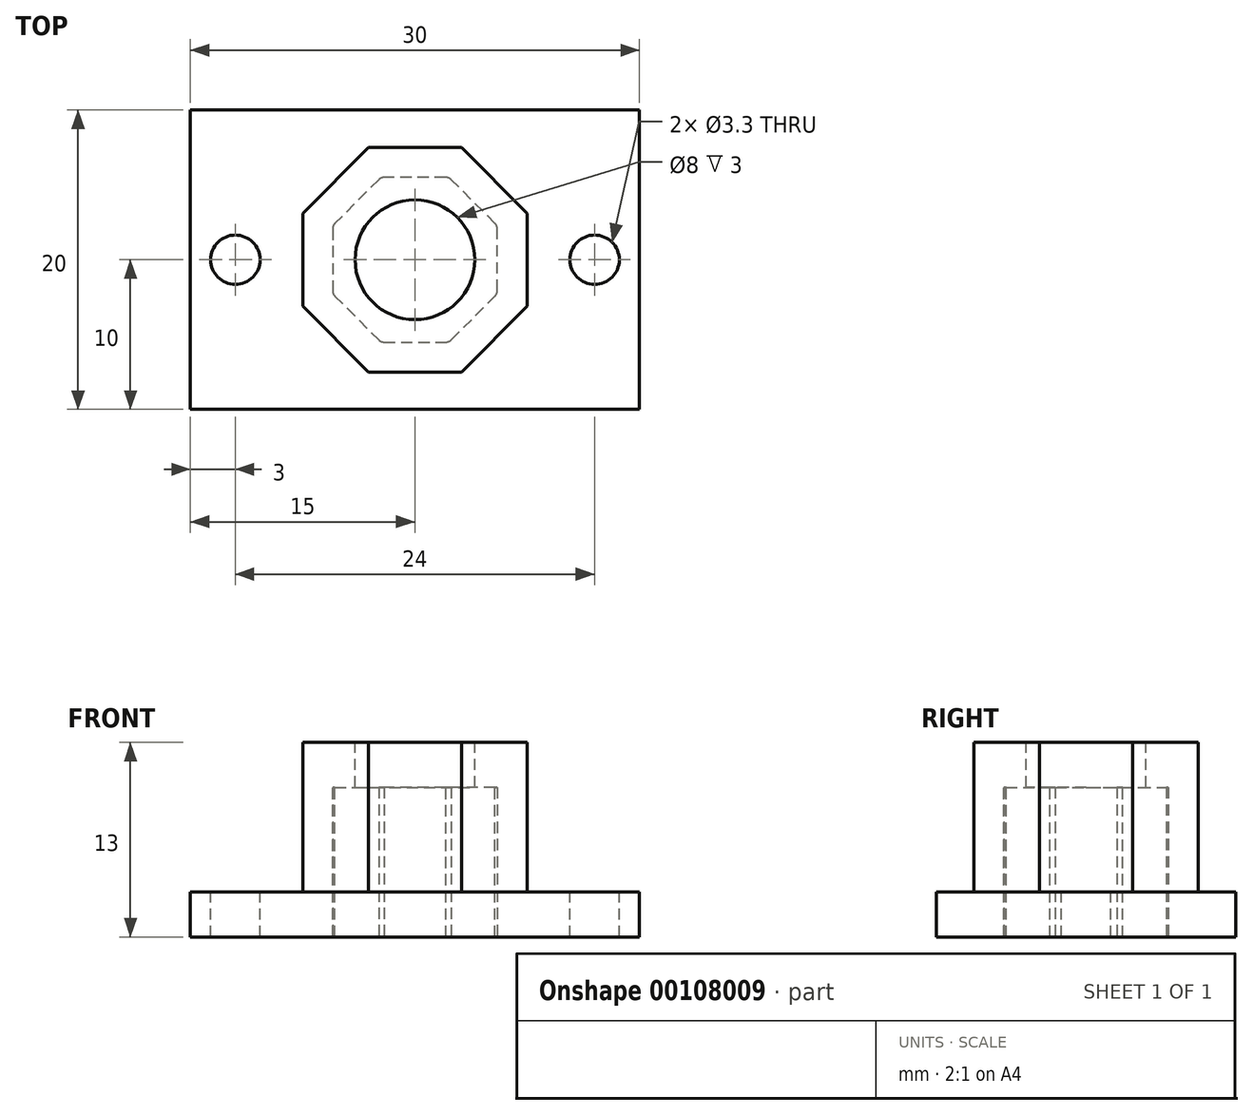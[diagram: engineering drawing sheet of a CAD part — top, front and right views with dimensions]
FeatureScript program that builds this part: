
annotation { "Feature Type Name" : "Feature", "Feature Type Description" : "" }
export const myFeature = defineFeature(function(context is Context, id is Id, definition is map)
    precondition{}
    {
        {
            var Q0;
            Q0=qCreatedBy(makeId("Front.planeOp"),FACE);
            var sketch = newSketch(context, id + "F0", { "sketchPlane" : qUnion([Q0])});
            skLineSegment(sketch, "E0.bottom", {"start": v(15, -1.5) * mm, "end": v(-15, -1.5) * mm});
            skLineSegment(sketch, "E0.top", {"start": v(15, 1.5) * mm, "end": v(-15, 1.5) * mm});
            skLineSegment(sketch, "E0.left", {"start": v(15, -1.5) * mm, "end": v(15, 1.5) * mm});
            skLineSegment(sketch, "E0.right", {"start": v(-15, -1.5) * mm, "end": v(-15, 1.5) * mm});
            skPoint(sketch, "E0.middle", {"position": v(0, 0) * mm});
            skSolve(sketch);
        }
        {
            var Q0;
            Q0 = qSketchRegion(id + "F0", true);
            var Q1;
            Q1 = qSketchRegion(id + "F6", true);
            extrude(context, id + "F1", {"entities" : qUnion([Q0, Q1]), "endBound" : BoundingType.SYMMETRIC, "depth" : 20 * mm});
        }
        {
            var Q0;
            Q0=makeQuery(id+"F1.opExtrude","SWEPT_FACE",FACE,{"disambiguationData":[OSD([sQuery(id+"F0.wireOp",EDGE,"E0.top")])]});
            var sketch = newSketch(context, id + "F2", { "sketchPlane" : qUnion([Q0])});
            skPoint(sketch, "E1", {"position": v(0, 0) * mm});
            skCircle(sketch, "E2.cCircle", {"center": v(0, 0) * mm, "radius": 7.5 * mm, "construction": true});
            skLineSegment(sketch, "E2.0", {"start": v(3.1, -7.5) * mm, "end": v(-3.1, -7.5) * mm});
            skLineSegment(sketch, "E2.1", {"start": v(-3.1, -7.5) * mm, "end": v(-7.5, -3.1) * mm});
            skLineSegment(sketch, "E2.2", {"start": v(-7.5, -3.1) * mm, "end": v(-7.5, 3.1) * mm});
            skLineSegment(sketch, "E2.3", {"start": v(-7.5, 3.1) * mm, "end": v(-3.1, 7.5) * mm});
            skLineSegment(sketch, "E2.4", {"start": v(-3.1, 7.5) * mm, "end": v(3.1, 7.5) * mm});
            skLineSegment(sketch, "E2.5", {"start": v(3.1, 7.5) * mm, "end": v(7.5, 3.1) * mm});
            skLineSegment(sketch, "E2.6", {"start": v(7.5, 3.1) * mm, "end": v(7.5, -3.1) * mm});
            skLineSegment(sketch, "E2.7", {"start": v(7.5, -3.1) * mm, "end": v(3.1, -7.5) * mm});
            skPoint(sketch, "E2.0.midPoint", {"position": v(0, -7.5) * mm});
            skSolve(sketch);
        }
        {
            var Q0;
            Q0 = qSketchRegion(id + "F2", true);
            extrude(context, id + "F3", {"entities" : qUnion([Q0]), "operationType" : NewBodyOperationType.ADD, "depth" : 10 * mm});
        }
        {
            var Q0;
            Q0=makeQuery(id+"F1.opExtrude","SWEPT_FACE",FACE,{"disambiguationData":[OSD([sQuery(id+"F0.wireOp",EDGE,"E0.bottom")])]});
            var sketch = newSketch(context, id + "F4", { "sketchPlane" : qUnion([Q0])});
            skCircle(sketch, "E3.cCircle", {"center": v(0, 0) * mm, "radius": 5.5 * mm, "construction": true});
            skLineSegment(sketch, "E3.0", {"start": v(2.28, -5.5) * mm, "end": v(-2.28, -5.5) * mm});
            skLineSegment(sketch, "E3.1", {"start": v(-2.28, -5.5) * mm, "end": v(-5.5, -2.28) * mm});
            skLineSegment(sketch, "E3.2", {"start": v(-5.5, -2.28) * mm, "end": v(-5.5, 2.28) * mm});
            skLineSegment(sketch, "E3.3", {"start": v(-5.5, 2.28) * mm, "end": v(-2.28, 5.5) * mm});
            skLineSegment(sketch, "E3.4", {"start": v(-2.28, 5.5) * mm, "end": v(2.28, 5.5) * mm});
            skLineSegment(sketch, "E3.5", {"start": v(2.28, 5.5) * mm, "end": v(5.5, 2.28) * mm});
            skLineSegment(sketch, "E3.6", {"start": v(5.5, 2.28) * mm, "end": v(5.5, -2.28) * mm});
            skLineSegment(sketch, "E3.7", {"start": v(5.5, -2.28) * mm, "end": v(2.28, -5.5) * mm});
            skPoint(sketch, "E3.0.midPoint", {"position": v(0, -5.5) * mm});
            skSolve(sketch);
        }
        {
            var Q0;
            Q0=makeQuery(id+"F4.imprint","IMPRINT",FACE,{"disambiguationData":[TD([[makeQuery(id+"F4.imprint","IMPRINT",EDGE,{"derivedFrom":sQuery(id+"F4.wireOp",EDGE,"E3.0")}),-1.0]])]});
            extrude(context, id + "F5", {"entities" : qUnion([Q0]), "operationType" : NewBodyOperationType.REMOVE, "oppositeDirection" : true, "depth" : 10 * mm});
        }
        {
            var Q0;
            Q0=makeQuery(id+"F3.opExtrude","CAP_FACE",FACE,{"disambiguationData":[OSD([sQuery(id+"F2.wireOp",EDGE,"E2.0"),sQuery(id+"F2.wireOp",EDGE,"E2.1"),sQuery(id+"F2.wireOp",EDGE,"E2.2"),sQuery(id+"F2.wireOp",EDGE,"E2.3"),sQuery(id+"F2.wireOp",EDGE,"E2.4"),sQuery(id+"F2.wireOp",EDGE,"E2.5"),sQuery(id+"F2.wireOp",EDGE,"E2.6"),sQuery(id+"F2.wireOp",EDGE,"E2.7")])],"isStart":false});
            var sketch = newSketch(context, id + "F6", { "sketchPlane" : qUnion([Q0])});
            skCircle(sketch, "E4", {"center": v(0, 0) * mm, "radius": 4 * mm});
            skSolve(sketch);
        }
        {
            var Q0;
            Q0=sQuery(id+"F6.wireOp",VERTEX,"E4.center");
            var Q1;
            Q1=makeQuery(id+"F1.opExtrude","SWEPT_BODY",BODY,{"disambiguationData":[OSD([sQuery(id+"F0.wireOp",EDGE,"E0.bottom"),sQuery(id+"F0.wireOp",EDGE,"E0.top"),sQuery(id+"F0.wireOp",EDGE,"E0.left"),sQuery(id+"F0.wireOp",EDGE,"E0.right")])]});
            hole(context, id + "F7", {"style" : HoleStyle.SIMPLE, "endStyle" : HoleEndStyle.THROUGH, "holeDiameter" : 8 * mm, "startFromSketch" : true, "locations" : qUnion([Q0]), "scope" : qUnion([Q1]), "isTappedThrough" : true});
        }
        {
            var Q0;
            Q0=makeQuery(id+"F5.boolean.opBoolean","COPY",EDGE,{"derivedFrom":makeQuery(id+"F5.opExtrude","SWEPT_EDGE",EDGE,{"disambiguationData":[OSD([sQuery(id+"F4.wireOp",EDGE,"E3.4"),sQuery(id+"F4.wireOp",EDGE,"E3.5")])]})});
            fillet(context, id + "F8", {"entities" : qUnion([Q0]), "radius" : 0.5 * mm, "rho" : 0.5, "crossSection" : FilletCrossSection.CONIC, "allowEdgeOverflow" : false});
        }
        {
            var Q0;
            Q0=makeQuery(id+"F5.boolean.opBoolean","COPY",EDGE,{"derivedFrom":makeQuery(id+"F5.opExtrude","SWEPT_EDGE",EDGE,{"disambiguationData":[OSD([sQuery(id+"F4.wireOp",EDGE,"E3.5"),sQuery(id+"F4.wireOp",EDGE,"E3.6")])]})});
            fillet(context, id + "F9", {"entities" : qUnion([Q0]), "radius" : 0.5 * mm, "tangentPropagation" : true, "allowEdgeOverflow" : false});
        }
        {
            var Q0;
            Q0=makeQuery(id+"F5.boolean.opBoolean","COPY",EDGE,{"derivedFrom":makeQuery(id+"F5.opExtrude","SWEPT_EDGE",EDGE,{"disambiguationData":[OSD([sQuery(id+"F4.wireOp",EDGE,"E3.3"),sQuery(id+"F4.wireOp",EDGE,"E3.4")])]})});
            fillet(context, id + "F10", {"entities" : qUnion([Q0]), "radius" : 0.5 * mm, "tangentPropagation" : true, "rho" : 0.5, "crossSection" : FilletCrossSection.CONIC, "allowEdgeOverflow" : false});
        }
        {
            var Q0;
            Q0=makeQuery(id+"F5.boolean.opBoolean","COPY",EDGE,{"derivedFrom":makeQuery(id+"F5.opExtrude","SWEPT_EDGE",EDGE,{"disambiguationData":[OSD([sQuery(id+"F4.wireOp",EDGE,"E3.2"),sQuery(id+"F4.wireOp",EDGE,"E3.3")])]})});
            fillet(context, id + "F11", {"entities" : qUnion([Q0]), "radius" : 0.5 * mm, "tangentPropagation" : true, "rho" : 0.5, "crossSection" : FilletCrossSection.CONIC, "allowEdgeOverflow" : false});
        }
        {
            var Q0;
            Q0=makeQuery(id+"F5.boolean.opBoolean","COPY",EDGE,{"derivedFrom":makeQuery(id+"F5.opExtrude","SWEPT_EDGE",EDGE,{"disambiguationData":[OSD([sQuery(id+"F4.wireOp",EDGE,"E3.1"),sQuery(id+"F4.wireOp",EDGE,"E3.2")])]})});
            fillet(context, id + "F12", {"entities" : qUnion([Q0]), "radius" : 0.5 * mm, "tangentPropagation" : true, "rho" : 0.5, "crossSection" : FilletCrossSection.CONIC, "allowEdgeOverflow" : false});
        }
        {
            var Q0;
            Q0=makeQuery(id+"F5.boolean.opBoolean","COPY",EDGE,{"derivedFrom":makeQuery(id+"F5.opExtrude","SWEPT_EDGE",EDGE,{"disambiguationData":[OSD([sQuery(id+"F4.wireOp",EDGE,"E3.6"),sQuery(id+"F4.wireOp",EDGE,"E3.7")])]})});
            fillet(context, id + "F13", {"entities" : qUnion([Q0]), "radius" : 0.5 * mm, "tangentPropagation" : true, "rho" : 0.5, "crossSection" : FilletCrossSection.CONIC, "allowEdgeOverflow" : false});
        }
        {
            var Q0;
            Q0=makeQuery(id+"F5.boolean.opBoolean","COPY",EDGE,{"derivedFrom":makeQuery(id+"F5.opExtrude","SWEPT_EDGE",EDGE,{"disambiguationData":[OSD([sQuery(id+"F4.wireOp",EDGE,"E3.0"),sQuery(id+"F4.wireOp",EDGE,"E3.7")])]})});
            fillet(context, id + "F14", {"entities" : qUnion([Q0]), "radius" : 0.5 * mm, "tangentPropagation" : true, "rho" : 0.5, "crossSection" : FilletCrossSection.CONIC, "allowEdgeOverflow" : false});
        }
        {
            var Q0;
            Q0=makeQuery(id+"F5.boolean.opBoolean","COPY",EDGE,{"derivedFrom":makeQuery(id+"F5.opExtrude","SWEPT_EDGE",EDGE,{"disambiguationData":[OSD([sQuery(id+"F4.wireOp",EDGE,"E3.0"),sQuery(id+"F4.wireOp",EDGE,"E3.1")])]})});
            fillet(context, id + "F15", {"entities" : qUnion([Q0]), "radius" : 0.5 * mm, "tangentPropagation" : true, "rho" : 0.5, "crossSection" : FilletCrossSection.CONIC, "allowEdgeOverflow" : false});
        }
        {
            var Q0;
            Q0=makeQuery(id+"F1.opExtrude","SWEPT_FACE",FACE,{"disambiguationData":[OSD([sQuery(id+"F0.wireOp",EDGE,"E0.top")])]});
            var sketch = newSketch(context, id + "F16", { "sketchPlane" : qUnion([Q0])});
            skPoint(sketch, "E5", {"position": v(12, 0) * mm});
            skPoint(sketch, "E6", {"position": v(-12, 0) * mm});
            skLineSegment(sketch, "E7.bottom", {"start": v(12, -8) * mm, "end": v(-12, -8) * mm});
            skLineSegment(sketch, "E7.top", {"start": v(12, 8) * mm, "end": v(-12, 8) * mm});
            skLineSegment(sketch, "E7.left", {"start": v(12, -8) * mm, "end": v(12, 8) * mm});
            skLineSegment(sketch, "E7.right", {"start": v(-12, -8) * mm, "end": v(-12, 8) * mm});
            skPoint(sketch, "E7.middle", {"position": v(0, 0) * mm});
            skSolve(sketch);
        }
        {
            var Q0;
            Q0=sQuery(id+"F16.wireOp",VERTEX,"E6");
            var Q1;
            Q1=sQuery(id+"F16.wireOp",VERTEX,"E5");
            var Q2;
            Q2=makeQuery(id+"F1.opExtrude","SWEPT_BODY",BODY,{"disambiguationData":[OSD([sQuery(id+"F0.wireOp",EDGE,"E0.bottom"),sQuery(id+"F0.wireOp",EDGE,"E0.top"),sQuery(id+"F0.wireOp",EDGE,"E0.left"),sQuery(id+"F0.wireOp",EDGE,"E0.right")])]});
            hole(context, id + "F17", {"style" : HoleStyle.SIMPLE, "endStyle" : HoleEndStyle.THROUGH, "standardTappedOrClearance" : lookupTablePath({ "standard" : "ISO", "fit" : "Normal", "size" : "M3", "type" : "Clearance" }), "standardBlindInLast" : lookupTablePath({ "fit" : "Standard", "standard" : "ISO", "size" : "M3", "type" : "Clearance" }), "holeDiameter" : 3.3 * mm, "startFromSketch" : true, "locations" : qUnion([Q0, Q1]), "scope" : qUnion([Q2]), "isTappedThrough" : true});
        }
    });
